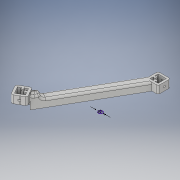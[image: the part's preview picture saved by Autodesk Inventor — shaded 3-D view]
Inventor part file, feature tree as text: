
AUTODESK INVENTOR PART (.ipt)
format: ipt  version: 2019 (Build 230136000, 136)  size: 513,536 bytes
history: native  units: mm
features: sketch x14, extrude x13, fillet x11
ambient origin geometry x8: Origin, YZ Plane, XZ Plane, XY Plane, X Axis, Y Axis, Z Axis, Center Point
bodies: Body1 (feature_tree)
feature tree (38):
  extrude  "Extrusion7"  TaperAngle=90.0deg  [1 undecoded]
  sketch  "Sketch7"  dims[d57=21.0mm d58=21.0mm d59=10.0mm]
  extrude  "Extrusion10"  Depth=21.0mm
  fillet  "Fillet2"  Radius=10.0mm
  extrude  "Extrusion11"  Depth=32.0mm
  extrude  "Extrusion13"  Depth=20.0mm TaperAngle=0.0deg
  fillet  "Fillet3"  Radius=10.0mm
  extrude  "Extrusion14"  TaperAngle=270.0deg  [1 undecoded]
  fillet  "Fillet4"  Radius=2.5mm
  fillet  "Fillet5"  Radius=2.5mm
  fillet  "Fillet6"  Radius=4.8mm
  fillet  "Fillet7"  Radius=10.0mm
  fillet  "Fillet8"  Radius=5.0mm
  fillet  "Fillet9"  [1 undecoded]
  fillet  "Fillet10"  Radius=5.0mm
  extrude  "Extrusion15"  Depth=10.5mm
  extrude  "Extrusion16"  Depth=1.0mm TaperAngle=360.0deg
  extrude  "Extrusion17"  Depth=0.5mm
  extrude  "Extrusion19"  TaperAngle=30.0deg  [1 undecoded]
  extrude  "Extrusion20"  Depth=4.8mm
  extrude  "Extrusion21"  TaperAngle=90.0deg  [1 undecoded]
  fillet  "Fillet11"  Radius=10.5mm
  fillet  "Fillet12"  Radius=1.0mm
  extrude  "Extrusion22"  TaperAngle=165.0deg  [1 undecoded]
  extrude  "Extrusion23"  Depth=1.0mm
  sketch  "Sketch6"  dims[d55=150.0mm d56=90.0deg]
  sketch  "Sketch10"  dims[d60=32.0mm d61=32.0mm]
  sketch  "Sketch11"  dims[d62=30.0mm d64=360.0deg d66=20.0mm d67=0.0mm d68=10.0mm]
  sketch  "Sketch13"  dims[d84=1.0mm d85=270.0deg d86=2.5mm d87=2.5mm d88=4.8mm d89=10.0mm d90=5.0mm d91=45.0deg d92=5.0mm]
  sketch  "Sketch14"  dims[d93=135.0deg d94=10.5mm]
  sketch  "Sketch15"  dims[d95=1.0mm d96=40.0mm d98=360.0deg]
  sketch  "Sketch16"  dims[d100=20.0mm d101=0.0mm d102=0.5mm]
  sketch  "Sketch17"  dims[d103=10.5mm d104=30.0deg]
  sketch  "Sketch18"  dims[d105=11.0mm d106=4.8mm]
  sketch  "Sketch19"  dims[d107=1.0mm d108=90.0deg d109=10.5mm d110=1.0mm]
  sketch  "Sketch20"  dims[d111=4.0mm d112=165.0deg]
  sketch  "Sketch21"  dims[d113=4.0mm d114=1.0mm]
  sketch  "Sketch22"  dims[d115=40.0mm d117=360.0deg d119=27.712813mm d120=27.712813mm d121=16.0mm d122=21.0mm d123=20.0mm d124=0.0mm d127=20.0mm d128=10.0mm d129=0.0mm d130=10.0mm d131=33.0mm d132=120.0deg d133=33.0mm d134=20.0mm d135=0.0mm d136=5.0mm d137=1.0mm d138=1.0mm d139=5.0mm d140=5.0mm d141=5.0mm d142=5.0mm d143=13.0mm d144=6.0mm d145=6.0mm d146=13.0mm d147=20.0mm d148=0.0mm d149=10.0mm d150=5.5mm d151=5.5mm d152=0.0mm d153=5.5mm d154=5.5mm d155=0.0mm d158=13.0mm d159=6.0mm d162=20.0mm d163=0.0mm d164=13.0mm d165=6.0mm d166=10.0mm d167=5.5mm d168=5.5mm d169=0.0mm d170=10.0mm d171=90.0deg d172=5.5mm d173=10.0mm d174=0.0mm d175=5.0mm d176=0.5mm d177=21.0mm d178=30.0deg d179=1.0mm d180=1.0mm d181=0.0mm d182=21.0mm d183=1.0mm d184=1.0mm d185=0.0mm]
note: 6 required parameter values undecoded (feature->parameter linkage not recoverable at this tier; creation-order binding heuristic only, values carry confidence <= 0.55)
